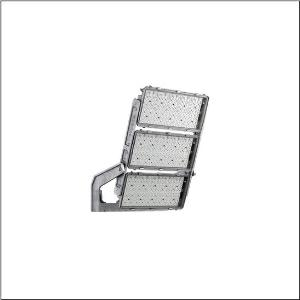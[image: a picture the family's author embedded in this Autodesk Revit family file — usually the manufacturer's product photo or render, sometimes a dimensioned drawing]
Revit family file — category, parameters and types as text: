
# Revit family: floodlight_fl_11_maxi_pro_remote___pl43_5xa779426a01aa_52e7
name_source: partatom
category: Lighting Fixtures
units: mm (PartAtom-declared; Revit-internal decimal feet)

## family parameters
Cut with Voids When Loaded = No
Host = Face
Light Source = No
Part Type = Normal
Room Calculation Point = No
Round Connector Dimension = Use Diameter
Shared = No

## types (1)
- --- (1 x LED, 172790 lm, 1387.6 W, 4000K)
    Apparent Load = 1388 VA
    CIE Flux Codes = 25 74 99 100 100
    Color Rendering = 70
    Color Temperature = 4000K
    Default Elevation = 1800 mm
    Description = Floodlight FL 11  maxi  pro Remote floodlight; light control with lens of PMMA; cover panel of toughened safety glass, transparent; light distribution: PL43, asymmetric direct distribution, LEDcolour temperature: 4000K, rated luminous flux: 172.790lm, colour rendering: CRI > 70, light colour: 740; luminous efficacy: 125lm/W; brightness control: DALI 2 (1 DALI address); with terminal, 8-pole, max. 2.5mm², mains connection: 220..240V/380..400V AC, 50/60Hz, surge voltage resistance: line to ground: 10kV, ECG replaceable separately, LED unit replaceable without ESD environment, dustproof LED module, dimming range 10..100%, no afterglow with DALI off / DMX off command; 1388W floodlight with 2x LED unit of diecast aluminium, coated grey; length: 713mm / width: 651mm / height: 338mm; mounting bracket, of diecast aluminium, uncoated, natural, equipment: Power, protection rating (complete): IP66; insulation class (complete): insulation class I (protective earthing); certification: CE, ENEC, VDE; ball protection: ball impact resistance with accessories, impact resistance: IK07; rated ambient temperature 10°C, only for outdoor installations, permissible operating ambient temperature: -40..+30°C, permissible storage temperature: -40..+85°Cpackaging unit: 1 piece

Light Distribution: PL43
    Height = 320 mm
    Lamp = 1 x LED
    Lamp Light Flux = 172790 lm
    Lamp Power = 1387.6 W
    Lamp count = 1
    Length = 1002 mm
    Luminous efficacy = 125 lm/W
    Manufacturer = Siteco
    ModVariant = No
    Model = 5XA779426A01AA
    Mounting Place = Ceiling
    Mounting Type = Surface mounted
    Number of Poles = 1
    OnlyDefault = Yes
    Power Factor = 1
    Product Name = Floodlight FL 11 maxi pro Remote | PL43
    Product group = floodlight | ceiling mounted
    ProductGroupID = 300
    Protection Class = Protection class I
    Protection Degree = IP 66
    RLX_Detail_Level = 1
    RLX_Emergency_Light_Flux = 0 lm
    RLX_Emergency_Type = 0
    RLX_Emergency_Type_DB = No
    RlxData = <blob elided: 52465 chars, md5=052adbb2>
    Socket = socket
    Standby Power = 0 W
    System Light Flux = 172790 lm
    System Power = 1388 W
    Type Comments = factory setting: luminous flux: 100 % | dim-lin: 254 | 955 mA
    Type Image = l_1349141.jpg
    URL = http://relux.com
    VarID = @adj_091656
    Voltage = 0 V
    Weight = 0.00 kg
    Width = 655 mm

## geometry (parser evidence)
native form markers: Blend x4, Sweep x13
no freeform markers — native parametric forms only
